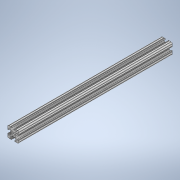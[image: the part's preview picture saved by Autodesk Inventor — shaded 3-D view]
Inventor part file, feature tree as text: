
AUTODESK INVENTOR PART (.ipt)
format: ipt  version: 2020 (Build 240168000, 168)  size: 236,544 bytes
history: native  units: in
note: dims shown in document units (in); Inventor stores cm internally (conversion verified against a paired STEP export)
features: extrude x1, sketch x1
ambient origin geometry x8: Origin, YZ Plane, XZ Plane, XY Plane, X Axis, Y Axis, Z Axis, Center Point
bodies: Solid1 (feature_tree)
feature tree (2):
  extrude  "Extrusion1"  [1 undecoded]
  sketch  "Sketch1"  dims[d0=14.0in d1=0.0in]
note: 1 required parameter value undecoded (feature->parameter linkage not recoverable at this tier; creation-order binding heuristic only, values carry confidence <= 0.55)
